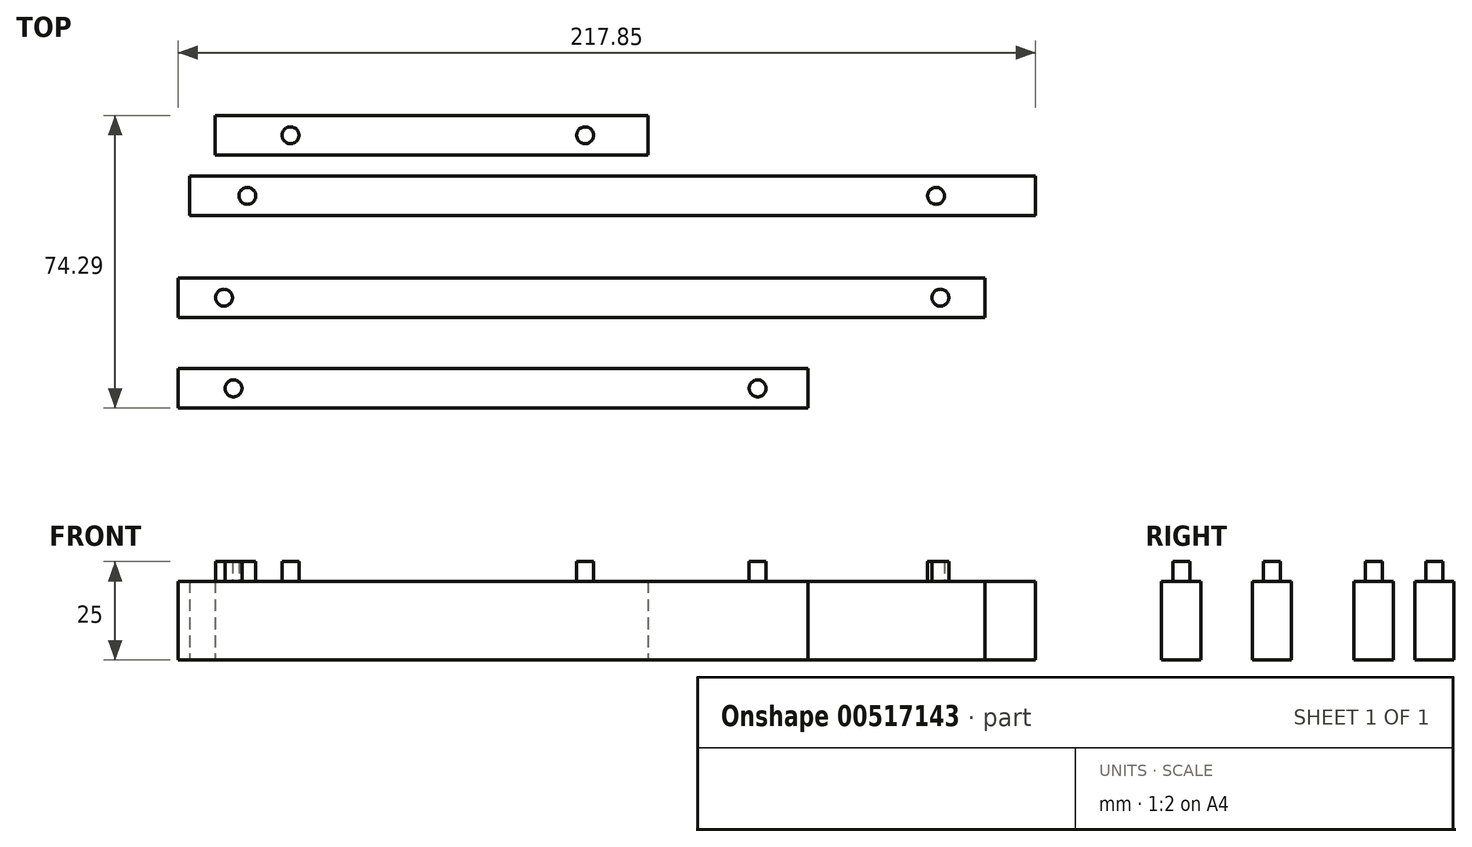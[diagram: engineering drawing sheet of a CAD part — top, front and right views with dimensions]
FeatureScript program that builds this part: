
annotation { "Feature Type Name" : "Feature", "Feature Type Description" : "" }
export const myFeature = defineFeature(function(context is Context, id is Id, definition is map)
    precondition{}
    {
        {
            var Q0;
            Q0=qCreatedBy(makeId("Top.planeOp"),FACE);
            var sketch = newSketch(context, id + "F0", { "sketchPlane" : qUnion([Q0])});
            skLineSegment(sketch, "E0", {"start": v(-57.3, 59.67) * mm, "end": v(52.7, 59.67) * mm});
            skLineSegment(sketch, "E1", {"start": v(-57.3, 59.67) * mm, "end": v(-57.3, 49.67) * mm});
            skLineSegment(sketch, "E2", {"start": v(-57.3, 49.67) * mm, "end": v(52.7, 49.67) * mm});
            skLineSegment(sketch, "E3", {"start": v(52.7, 49.67) * mm, "end": v(52.7, 59.67) * mm});
            skLineSegment(sketch, "E4", {"start": v(-63.86, 44.28) * mm, "end": v(151.14, 44.28) * mm});
            skLineSegment(sketch, "E5", {"start": v(-63.86, 44.28) * mm, "end": v(-63.86, 34.28) * mm});
            skLineSegment(sketch, "E6", {"start": v(-63.86, 34.28) * mm, "end": v(151.14, 34.28) * mm});
            skLineSegment(sketch, "E7", {"start": v(151.14, 34.28) * mm, "end": v(151.14, 44.28) * mm});
            skLineSegment(sketch, "E8", {"start": v(-66.7, 18.4) * mm, "end": v(138.3, 18.4) * mm});
            skLineSegment(sketch, "E9", {"start": v(-66.7, 18.4) * mm, "end": v(-66.7, 8.4) * mm});
            skLineSegment(sketch, "E10", {"start": v(-66.7, 8.4) * mm, "end": v(138.3, 8.4) * mm});
            skLineSegment(sketch, "E11", {"start": v(138.3, 8.4) * mm, "end": v(138.3, 18.4) * mm});
            skLineSegment(sketch, "E12", {"start": v(-66.7, -4.62) * mm, "end": v(93.3, -4.62) * mm});
            skLineSegment(sketch, "E13", {"start": v(-66.7, -4.62) * mm, "end": v(-66.7, -14.62) * mm});
            skLineSegment(sketch, "E14", {"start": v(-66.7, -14.62) * mm, "end": v(93.3, -14.62) * mm});
            skLineSegment(sketch, "E15", {"start": v(93.3, -14.62) * mm, "end": v(93.3, -4.62) * mm});
            skLineSegment(sketch, "E16", {"start": v(-57.3, 59.67) * mm, "end": v(-42.3, 59.67) * mm});
            skLineSegment(sketch, "E17", {"start": v(-42.3, 59.67) * mm, "end": v(-57.3, 59.67) * mm});
            skLineSegment(sketch, "E18", {"start": v(52.7, 59.67) * mm, "end": v(37.7, 59.67) * mm});
            skLineSegment(sketch, "E19", {"start": v(-42.3, 49.67) * mm, "end": v(38.57, 49.67) * mm});
            skLineSegment(sketch, "E20", {"start": v(38.57, 49.67) * mm, "end": v(52.7, 49.67) * mm});
            skLineSegment(sketch, "E21", {"start": v(151.14, 44.28) * mm, "end": v(136.14, 44.28) * mm});
            skLineSegment(sketch, "E22", {"start": v(136.14, 44.28) * mm, "end": v(151.14, 44.28) * mm});
            skLineSegment(sketch, "E23", {"start": v(-63.86, 44.28) * mm, "end": v(-48.86, 44.28) * mm});
            skLineSegment(sketch, "E24", {"start": v(-48.86, 34.28) * mm, "end": v(136.14, 34.28) * mm});
            skLineSegment(sketch, "E25", {"start": v(138.3, 13.4) * mm, "end": v(138.3, 18.4) * mm});
            skLineSegment(sketch, "E26", {"start": v(138.3, 18.4) * mm, "end": v(123.3, 18.4) * mm});
            skLineSegment(sketch, "E27", {"start": v(-66.7, 18.4) * mm, "end": v(-51.7, 18.4) * mm});
            skLineSegment(sketch, "E28", {"start": v(93.3, -9.62) * mm, "end": v(93.3, -4.62) * mm});
            skLineSegment(sketch, "E29", {"start": v(93.3, -4.62) * mm, "end": v(78.3, -4.62) * mm});
            skLineSegment(sketch, "E30", {"start": v(-66.7, -4.62) * mm, "end": v(-51.7, -4.62) * mm});
            skSolve(sketch);
        }
        {
            var Q0;
            Q0=makeQuery(id+"F0.imprint","IMPRINT",FACE,{"disambiguationData":[TD([[makeQuery(id+"F0.imprint","IMPRINT",EDGE,{"derivedFrom":sQuery(id+"F0.wireOp",EDGE,"E0")}),-1.0]])]});
            extrude(context, id + "F1", {"entities" : qUnion([Q0]), "depth" : 20 * mm, "offsetDistance" : 25 * mm});
        }
        {
            var Q0;
            Q0 = qSketchRegion(id + "F0", true);
            extrude(context, id + "F2", {"entities" : qUnion([Q0]), "operationType" : NewBodyOperationType.ADD, "depth" : 20 * mm, "offsetDistance" : 25 * mm});
        }
        {
            var Q0;
            Q0=makeQuery(id+"F1.opExtrude","CAP_FACE",FACE,{"disambiguationData":[OSD([sQuery(id+"F0.wireOp",EDGE,"E0"),sQuery(id+"F0.wireOp",EDGE,"E1"),sQuery(id+"F0.wireOp",EDGE,"E2"),sQuery(id+"F0.wireOp",EDGE,"E3"),sQuery(id+"F0.wireOp",EDGE,"E17"),sQuery(id+"F0.wireOp",EDGE,"E18"),sQuery(id+"F0.wireOp",EDGE,"E19"),sQuery(id+"F0.wireOp",EDGE,"E20")])],"isStart":false});
            var sketch = newSketch(context, id + "F3", { "sketchPlane" : qUnion([Q0])});
            skCircle(sketch, "E31", {"center": v(36.68, 54.67) * mm, "radius": 2.15 * mm});
            skCircle(sketch, "E32", {"center": v(-38.17, 54.67) * mm, "radius": 2.15 * mm});
            skSolve(sketch);
        }
        {
            var Q0;
            Q0=makeQuery(id+"F3.imprint","IMPRINT",FACE,{"disambiguationData":[TD([[makeQuery(id+"F3.imprint","IMPRINT",EDGE,{"derivedFrom":sQuery(id+"F3.wireOp",EDGE,"E32")}),1.0]])]});
            var Q1;
            Q1=makeQuery(id+"F3.imprint","IMPRINT",FACE,{"disambiguationData":[TD([[makeQuery(id+"F3.imprint","IMPRINT",EDGE,{"derivedFrom":sQuery(id+"F3.wireOp",EDGE,"E31")}),1.0]])]});
            extrude(context, id + "F4", {"entities" : qUnion([Q0, Q1]), "operationType" : NewBodyOperationType.ADD, "depth" : 5 * mm, "offsetDistance" : 25 * mm});
        }
        {
            var Q0;
            Q0=makeQuery(id+"F2.opExtrude","CAP_FACE",FACE,{"disambiguationData":[OSD([sQuery(id+"F0.wireOp",EDGE,"E4"),sQuery(id+"F0.wireOp",EDGE,"E5"),sQuery(id+"F0.wireOp",EDGE,"E6"),sQuery(id+"F0.wireOp",EDGE,"E7"),sQuery(id+"F0.wireOp",EDGE,"E22"),sQuery(id+"F0.wireOp",EDGE,"E23"),sQuery(id+"F0.wireOp",EDGE,"E24")])],"isStart":false});
            var sketch = newSketch(context, id + "F5", { "sketchPlane" : qUnion([Q0])});
            skCircle(sketch, "E33", {"center": v(-49.13, 39.28) * mm, "radius": 2.15 * mm});
            skCircle(sketch, "E34", {"center": v(125.83, 39.28) * mm, "radius": 2.15 * mm});
            skSolve(sketch);
        }
        {
            var Q0;
            Q0=makeQuery(id+"F5.imprint","IMPRINT",FACE,{"disambiguationData":[TD([[makeQuery(id+"F5.imprint","IMPRINT",EDGE,{"derivedFrom":sQuery(id+"F5.wireOp",EDGE,"E33")}),1.0]])]});
            var Q1;
            Q1=makeQuery(id+"F5.imprint","IMPRINT",FACE,{"disambiguationData":[TD([[makeQuery(id+"F5.imprint","IMPRINT",EDGE,{"derivedFrom":sQuery(id+"F5.wireOp",EDGE,"E34")}),1.0]])]});
            extrude(context, id + "F6", {"entities" : qUnion([Q0, Q1]), "operationType" : NewBodyOperationType.ADD, "depth" : 5 * mm, "offsetDistance" : 25 * mm});
        }
        {
            var Q0;
            Q0=makeQuery(id+"F2.opExtrude","CAP_FACE",FACE,{"disambiguationData":[OSD([sQuery(id+"F0.wireOp",EDGE,"E8"),sQuery(id+"F0.wireOp",EDGE,"E9"),sQuery(id+"F0.wireOp",EDGE,"E10"),sQuery(id+"F0.wireOp",EDGE,"E11"),sQuery(id+"F0.wireOp",EDGE,"E25"),sQuery(id+"F0.wireOp",EDGE,"E26"),sQuery(id+"F0.wireOp",EDGE,"E27")])],"isStart":false});
            var sketch = newSketch(context, id + "F7", { "sketchPlane" : qUnion([Q0])});
            skCircle(sketch, "E35", {"center": v(-55.07, 13.4) * mm, "radius": 2.15 * mm});
            skCircle(sketch, "E36", {"center": v(126.94, 13.4) * mm, "radius": 2.15 * mm});
            skSolve(sketch);
        }
        {
            var Q0;
            Q0=makeQuery(id+"F7.imprint","IMPRINT",FACE,{"disambiguationData":[TD([[makeQuery(id+"F7.imprint","IMPRINT",EDGE,{"derivedFrom":sQuery(id+"F7.wireOp",EDGE,"E35")}),1.0]])]});
            var Q1;
            Q1=makeQuery(id+"F7.imprint","IMPRINT",FACE,{"disambiguationData":[TD([[makeQuery(id+"F7.imprint","IMPRINT",EDGE,{"derivedFrom":sQuery(id+"F7.wireOp",EDGE,"E36")}),1.0]])]});
            extrude(context, id + "F8", {"entities" : qUnion([Q0, Q1]), "operationType" : NewBodyOperationType.ADD, "depth" : 5 * mm, "offsetDistance" : 25 * mm});
        }
        {
            var Q0;
            Q0=makeQuery(id+"F2.opExtrude","CAP_FACE",FACE,{"disambiguationData":[OSD([sQuery(id+"F0.wireOp",EDGE,"E12"),sQuery(id+"F0.wireOp",EDGE,"E13"),sQuery(id+"F0.wireOp",EDGE,"E14"),sQuery(id+"F0.wireOp",EDGE,"E15"),sQuery(id+"F0.wireOp",EDGE,"E28"),sQuery(id+"F0.wireOp",EDGE,"E29"),sQuery(id+"F0.wireOp",EDGE,"E30")])],"isStart":false});
            var sketch = newSketch(context, id + "F9", { "sketchPlane" : qUnion([Q0])});
            skCircle(sketch, "E37", {"center": v(-52.66, -9.62) * mm, "radius": 2.15 * mm});
            skCircle(sketch, "E38", {"center": v(80.5, -9.62) * mm, "radius": 2.15 * mm});
            skSolve(sketch);
        }
        {
            var Q0;
            Q0=makeQuery(id+"F9.imprint","IMPRINT",FACE,{"disambiguationData":[TD([[makeQuery(id+"F9.imprint","IMPRINT",EDGE,{"derivedFrom":sQuery(id+"F9.wireOp",EDGE,"E37")}),1.0]])]});
            var Q1;
            Q1=makeQuery(id+"F9.imprint","IMPRINT",FACE,{"disambiguationData":[TD([[makeQuery(id+"F9.imprint","IMPRINT",EDGE,{"derivedFrom":sQuery(id+"F9.wireOp",EDGE,"E38")}),1.0]])]});
            extrude(context, id + "F10", {"entities" : qUnion([Q0, Q1]), "operationType" : NewBodyOperationType.ADD, "depth" : 5 * mm, "offsetDistance" : 25 * mm});
        }
    });
